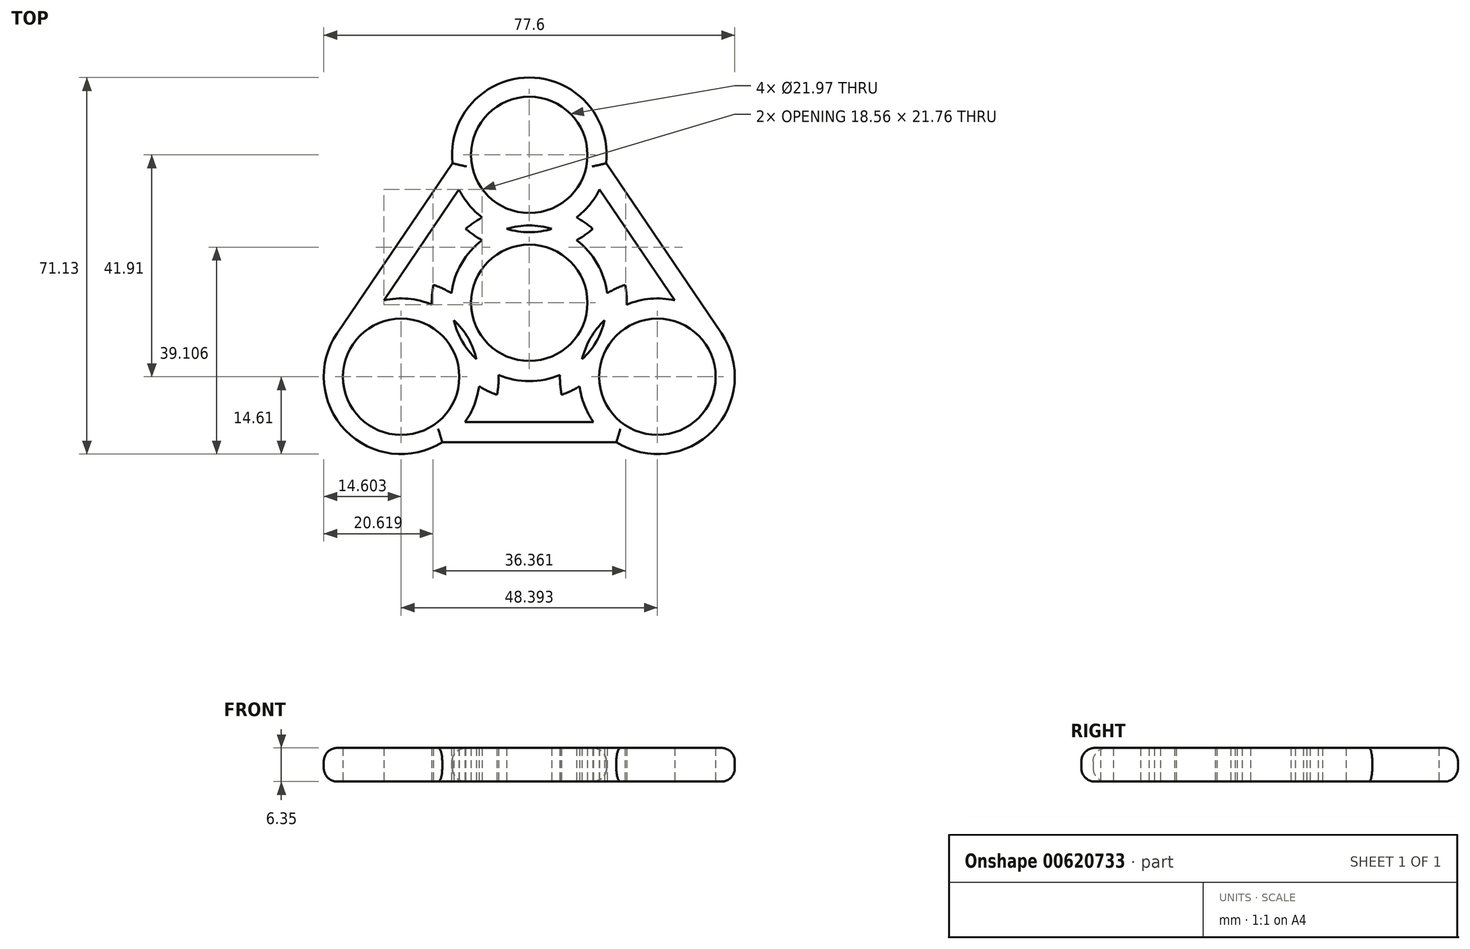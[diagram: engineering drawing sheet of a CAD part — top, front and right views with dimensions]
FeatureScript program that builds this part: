
annotation { "Feature Type Name" : "Feature", "Feature Type Description" : "" }
export const myFeature = defineFeature(function(context is Context, id is Id, definition is map)
    precondition{}
    {
        {
            var Q0;
            Q0=qCreatedBy(makeId("Top.planeOp"),FACE);
            var sketch = newSketch(context, id + "F0", { "sketchPlane" : qUnion([Q0])});
            skCircle(sketch, "E0", {"center": v(0, 0) * mm, "radius": 10.99 * mm});
            skLineSegment(sketch, "E1", {"start": v(0, 27.94) * mm, "end": v(0, 0) * mm});
            skLineSegment(sketch, "E2", {"start": v(0, 0) * mm, "end": v(-24.2, -13.97) * mm});
            skLineSegment(sketch, "E3", {"start": v(0, 0) * mm, "end": v(24.2, -13.97) * mm});
            skCircle(sketch, "E4", {"center": v(0, 27.94) * mm, "radius": 10.99 * mm});
            skCircle(sketch, "E5", {"center": v(24.2, -13.97) * mm, "radius": 10.99 * mm});
            skCircle(sketch, "E6", {"center": v(-24.2, -13.97) * mm, "radius": 10.99 * mm});
            skCircle(sketch, "E7", {"center": v(0, 27.94) * mm, "radius": 14.6 * mm});
            skCircle(sketch, "E8", {"center": v(-24.2, -13.97) * mm, "radius": 14.6 * mm});
            skCircle(sketch, "E9", {"center": v(24.2, -13.97) * mm, "radius": 14.6 * mm});
            skCircle(sketch, "E10", {"center": v(0, 0) * mm, "radius": 14.6 * mm});
            skLineSegment(sketch, "E11", {"start": v(14.52, 26.36) * mm, "end": v(36.29, -5.78) * mm});
            skLineSegment(sketch, "E12", {"start": v(-14.52, 26.36) * mm, "end": v(-36.29, -5.78) * mm});
            skLineSegment(sketch, "E13", {"start": v(-16.44, -26.34) * mm, "end": v(16.44, -26.34) * mm});
            skSolve(sketch);
        }
        {
            var Q0;
            Q0 = qSketchRegion(id + "F0", true);
            var Q1;
            {var subQ1=sQuery(id+"F0.wireOp",EDGE,"E2");var subQ6=sQuery(id+"F0.wireOp",EDGE,"E0");var subQ10=makeQuery(id+"F0.imprint","INTERSECT",VERTEX,{"derivedFrom":[subQ6,subQ1]});Q1=makeQuery(id+"F0.imprint","IMPRINT",FACE,{"disambiguationData":[TD([[makeQuery(id+"F0.imprint","IMPRINT",EDGE,{"disambiguationData":[TD([[subQ10,-1.0]])],"derivedFrom":subQ6}),-1.0]])]});}
            var Q2;
            {var subQ5=sQuery(id+"F0.wireOp",EDGE,"E2");var subQ6=sQuery(id+"F0.wireOp",EDGE,"E0");var subQ7=makeQuery(id+"F0.imprint","INTERSECT",VERTEX,{"derivedFrom":[subQ6,subQ5]});Q2=makeQuery(id+"F0.imprint","IMPRINT",FACE,{"disambiguationData":[TD([[makeQuery(id+"F0.imprint","IMPRINT",EDGE,{"disambiguationData":[TD([[subQ7,1.0]])],"derivedFrom":subQ6}),-1.0]])]});}
            var Q3;
            {var subQ1=sQuery(id+"F0.wireOp",EDGE,"E0");var subQ5=sQuery(id+"F0.wireOp",EDGE,"E1");var subQ6=makeQuery(id+"F0.imprint","INTERSECT",VERTEX,{"derivedFrom":[subQ1,subQ5]});Q3=makeQuery(id+"F0.imprint","IMPRINT",FACE,{"disambiguationData":[TD([[makeQuery(id+"F0.imprint","IMPRINT",EDGE,{"disambiguationData":[TD([[subQ6,1.0]])],"derivedFrom":subQ1}),-1.0]])]});}
            extrude(context, id + "F1", {"entities" : qUnion([Q0, Q1, Q2, Q3]), "depth" : 6.35 * mm, "offsetDistance" : 25.4 * mm});
        }
        {
            var Q0;
            Q0=makeQuery(id+"F1.opExtrude","CAP_EDGE",EDGE,{"disambiguationData":[OSD([sQuery(id+"F0.wireOp",EDGE,"E11")])],"isStart":false});
            var Q1;
            Q1=makeQuery(id+"F1.opExtrude","CAP_EDGE",EDGE,{"disambiguationData":[OSD([sQuery(id+"F0.wireOp",EDGE,"E13")])],"isStart":false});
            var Q2;
            {var subQ0=sQuery(id+"F0.wireOp",EDGE,"E9");Q2=makeQuery(id+"F1.opExtrude","CAP_EDGE",EDGE,{"disambiguationData":[OSD([subQ0]),TDD([makeQuery(id+"F0.imprint","IMPRINT",EDGE,{"disambiguationData":[TD([[makeQuery(id+"F0.imprint","INTERSECT",VERTEX,{"derivedFrom":[subQ0,sQuery(id+"F0.wireOp",EDGE,"E11")]}),1.0]])],"derivedFrom":subQ0})])],"isStart":false});}
            var Q3;
            {var subQ0=sQuery(id+"F0.wireOp",EDGE,"E8");Q3=makeQuery(id+"F1.opExtrude","CAP_EDGE",EDGE,{"disambiguationData":[OSD([subQ0]),TDD([makeQuery(id+"F0.imprint","IMPRINT",EDGE,{"disambiguationData":[TD([[makeQuery(id+"F0.imprint","INTERSECT",VERTEX,{"derivedFrom":[subQ0,sQuery(id+"F0.wireOp",EDGE,"E12")]}),-1.0]])],"derivedFrom":subQ0})])],"isStart":false});}
            var Q4;
            {var subQ0=sQuery(id+"F0.wireOp",EDGE,"E7");Q4=makeQuery(id+"F1.opExtrude","CAP_EDGE",EDGE,{"disambiguationData":[OSD([subQ0]),TDD([makeQuery(id+"F0.imprint","IMPRINT",EDGE,{"disambiguationData":[TD([[makeQuery(id+"F0.imprint","INTERSECT",VERTEX,{"derivedFrom":[subQ0,sQuery(id+"F0.wireOp",EDGE,"E11")]}),-1.0]])],"derivedFrom":subQ0})])],"isStart":false});}
            fillet(context, id + "F2", {"entities" : qUnion([Q0, Q1, Q2, Q3, Q4]), "radius" : 2.54 * mm, "tangentPropagation" : true, "allowEdgeOverflow" : false});
        }
        {
            var Q0;
            Q0=makeQuery(id+"F1.opExtrude","CAP_EDGE",EDGE,{"disambiguationData":[OSD([sQuery(id+"F0.wireOp",EDGE,"E13")])],"isStart":true});
            var Q1;
            {var subQ0=sQuery(id+"F0.wireOp",EDGE,"E8");Q1=makeQuery(id+"F1.opExtrude","CAP_EDGE",EDGE,{"disambiguationData":[OSD([subQ0]),TDD([makeQuery(id+"F0.imprint","IMPRINT",EDGE,{"disambiguationData":[TD([[makeQuery(id+"F0.imprint","INTERSECT",VERTEX,{"derivedFrom":[subQ0,sQuery(id+"F0.wireOp",EDGE,"E12")]}),-1.0]])],"derivedFrom":subQ0})])],"isStart":true});}
            var Q2;
            Q2=makeQuery(id+"F1.opExtrude","CAP_EDGE",EDGE,{"disambiguationData":[OSD([sQuery(id+"F0.wireOp",EDGE,"E11")])],"isStart":true});
            var Q3;
            {var subQ0=sQuery(id+"F0.wireOp",EDGE,"E7");Q3=makeQuery(id+"F1.opExtrude","CAP_EDGE",EDGE,{"disambiguationData":[OSD([subQ0]),TDD([makeQuery(id+"F0.imprint","IMPRINT",EDGE,{"disambiguationData":[TD([[makeQuery(id+"F0.imprint","INTERSECT",VERTEX,{"derivedFrom":[subQ0,sQuery(id+"F0.wireOp",EDGE,"E11")]}),-1.0]])],"derivedFrom":subQ0})])],"isStart":true});}
            fillet(context, id + "F3", {"entities" : qUnion([Q0, Q1, Q2, Q3]), "radius" : 2.54 * mm, "tangentPropagation" : true, "allowEdgeOverflow" : false});
        }
        {
            var Q0;
            Q0=makeQuery(id+"F1.opExtrude","CAP_FACE",FACE,{"disambiguationData":[OSD([sQuery(id+"F0.wireOp",EDGE,"E0"),sQuery(id+"F0.wireOp",EDGE,"E4"),sQuery(id+"F0.wireOp",EDGE,"E5"),sQuery(id+"F0.wireOp",EDGE,"E6"),sQuery(id+"F0.wireOp",EDGE,"E7"),sQuery(id+"F0.wireOp",EDGE,"E8"),sQuery(id+"F0.wireOp",EDGE,"E9"),sQuery(id+"F0.wireOp",EDGE,"E10"),sQuery(id+"F0.wireOp",EDGE,"E11"),sQuery(id+"F0.wireOp",EDGE,"E12"),sQuery(id+"F0.wireOp",EDGE,"E13")])],"isStart":true});
            var Q1;
            Q1=makeQuery(id+"F1.opExtrude","CAP_FACE",FACE,{"disambiguationData":[OSD([sQuery(id+"F0.wireOp",EDGE,"E0"),sQuery(id+"F0.wireOp",EDGE,"E4"),sQuery(id+"F0.wireOp",EDGE,"E5"),sQuery(id+"F0.wireOp",EDGE,"E6"),sQuery(id+"F0.wireOp",EDGE,"E7"),sQuery(id+"F0.wireOp",EDGE,"E8"),sQuery(id+"F0.wireOp",EDGE,"E9"),sQuery(id+"F0.wireOp",EDGE,"E10"),sQuery(id+"F0.wireOp",EDGE,"E11"),sQuery(id+"F0.wireOp",EDGE,"E12"),sQuery(id+"F0.wireOp",EDGE,"E13")])],"isStart":false});
            shell(context, id + "F4", {"entities" : qUnion([Q0, Q1]), "thickness" : 3.8 * mm});
        }
    });
